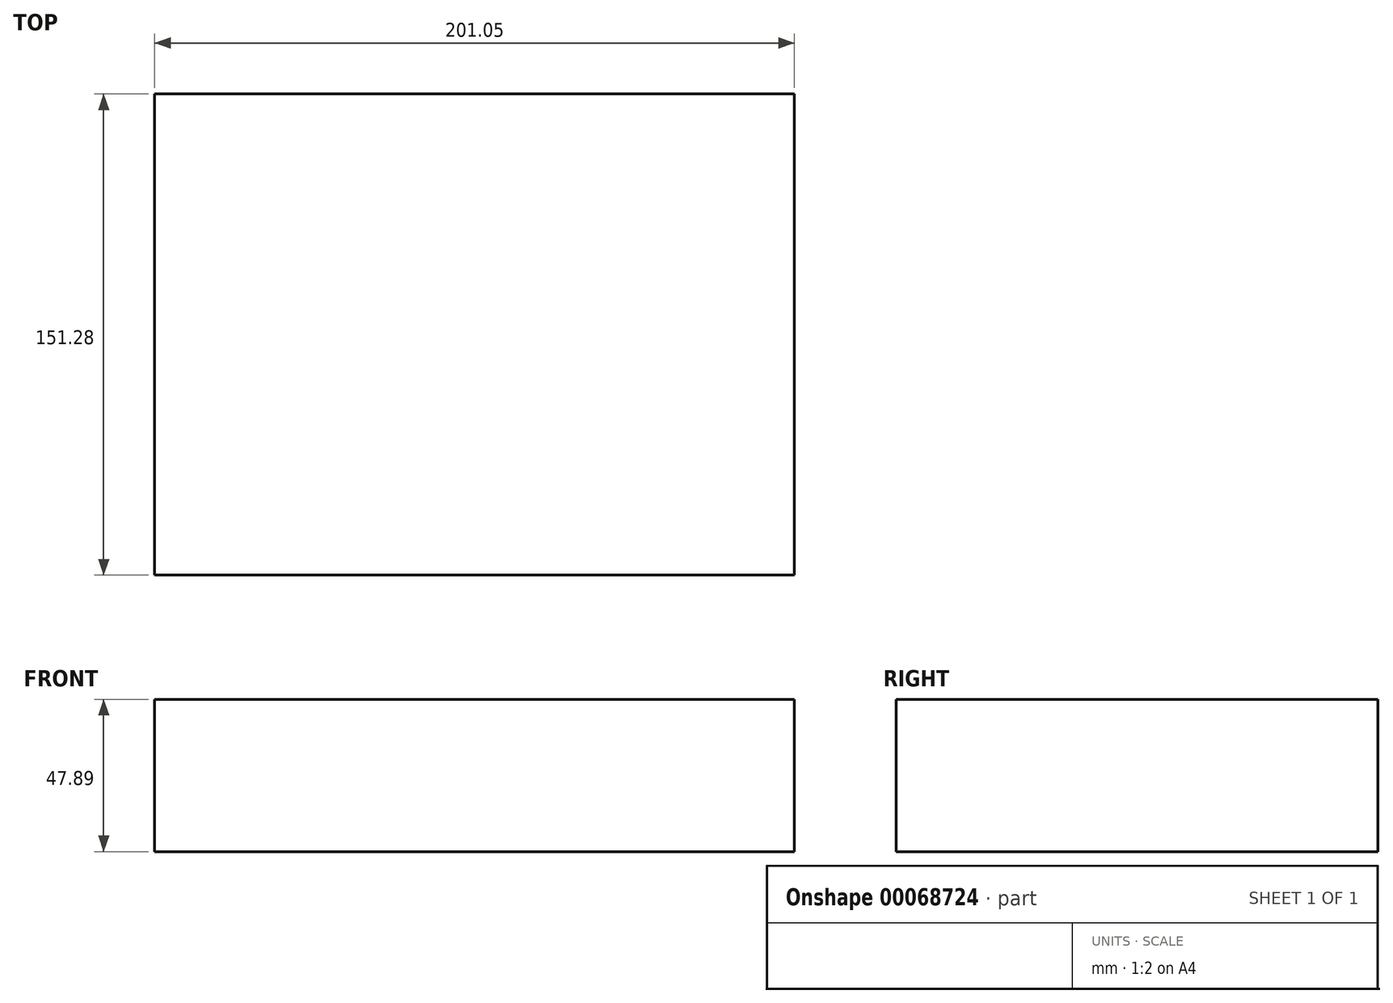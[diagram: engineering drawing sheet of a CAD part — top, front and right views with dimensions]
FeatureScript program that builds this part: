
annotation { "Feature Type Name" : "Feature", "Feature Type Description" : "" }
export const myFeature = defineFeature(function(context is Context, id is Id, definition is map)
    precondition{}
    {
        {
            var Q0;
            Q0=qCreatedBy(makeId("Top.planeOp"),FACE);
            var sketch = newSketch(context, id + "F0", { "sketchPlane" : qUnion([Q0])});
            skLineSegment(sketch, "E0.bottom", {"start": v(87.43, -14.78) * mm, "end": v(-113.62, -14.78) * mm});
            skLineSegment(sketch, "E0.top", {"start": v(87.43, 136.5) * mm, "end": v(-113.62, 136.5) * mm});
            skLineSegment(sketch, "E0.left", {"start": v(87.43, -14.78) * mm, "end": v(87.43, 136.5) * mm});
            skLineSegment(sketch, "E0.right", {"start": v(-113.62, -14.78) * mm, "end": v(-113.62, 136.5) * mm});
            skLineSegment(sketch, "E1.bottom", {"start": v(-113.62, 136.5) * mm, "end": v(3.64, 136.5) * mm, "construction": true});
            skLineSegment(sketch, "E1.top", {"start": v(-113.62, -14.78) * mm, "end": v(3.64, -14.78) * mm, "construction": true});
            skLineSegment(sketch, "E1.left", {"start": v(-113.62, 136.5) * mm, "end": v(-113.62, -14.78) * mm, "construction": true});
            skLineSegment(sketch, "E1.right", {"start": v(3.64, 136.5) * mm, "end": v(3.64, -14.78) * mm, "construction": true});
            skSolve(sketch);
        }
        {
            var Q0;
            Q0=makeQuery(id+"F0.imprint","IMPRINT",FACE,{"disambiguationData":[TD([[makeQuery(id+"F0.imprint","IMPRINT",EDGE,{"derivedFrom":sQuery(id+"F0.wireOp",EDGE,"E0.bottom")}),-1.0]])]});
            extrude(context, id + "F1", {"entities" : qUnion([Q0]), "depth" : 47.9 * mm});
        }
    });
